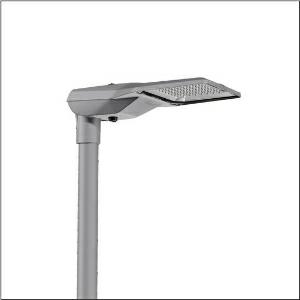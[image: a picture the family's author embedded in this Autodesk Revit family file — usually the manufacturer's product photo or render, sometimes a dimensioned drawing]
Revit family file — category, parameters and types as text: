
# Revit family: streetlight_sl_21_midi___st1_0ab_5xe3m33t08mb_b6c0
name_source: partatom
category: Lighting Fixtures
units: mm (PartAtom-declared; Revit-internal decimal feet)

## family parameters
Cut with Voids When Loaded = No
Host = Face
Light Source = No
Part Type = Normal
Room Calculation Point = No
Round Connector Dimension = Use Diameter
Shared = No

## types (1)
- --- (1 x LED, 16080 lm, 136 W, 3000K)
    Apparent Load = 136 VA
    CIE Flux Codes = 38 73 97 100 100
    Color Rendering = 70
    Color Temperature = 3000K
    Default Elevation = 1800 mm
    Description = Streetlight SL 21 midi, mast luminaire, primary light control with lens, of PMMA, primary optical cover: cover, of toughened safety glass, transparent, light distribution: ST1.0aB, light emission: direct distribution, primary light characteristic: asymmetric, installation type: side-entry, post-top, LED, High Power LED, rated luminous flux: 16.080lm, luminous efficacy: 118lm/W, light colour: 730, colour temperature: 3000K, control gear: D4i, control: flexible luminous flux parameterisation, time-dependent luminous flux control, constant luminous flux control, overheat protection, pre-setting: logarithmic dimming characteristic, mains connection: 230..240V, AC, 50/60Hz, start of lifetime: 136W, end of service life: 142W, reduction: 61W, luminaire housing, of diecast aluminium, powder-coated, Siteco® metallic grey (DB 702S), corrosivity category C5 mid according to DIN EN ISO 12944, please order mast flange separately, inclination adjustable: 0°, 5°, 10°, 15°, sealing non-destructively replaceable, multi-level sealing system, length: 644mm, width: 335mm, height: 110mm, mast flange for spigot size: 42mm (side-entry): 5XC10008XM4, 60/48mm (side-entry/post-top): 5XC10108XM2, 76/60mm (side-entry/post-top): 5XC10108XM1, mounting height: 4..8m, Smart Interface below and above, protection rating (complete): IP66, insulation class (complete): insulation class II (safety insulation), certification: CE, ENEC, ENEC+, VDE, impact resistance: IK10, permissible operating ambient temperature for outdoor applications: -40..+50°C, standard-compliant lighting for roads and squares, packaging unit: 1 piece

Light Distribution: ST1.0aB
    Height = 111 mm
    Lamp = 1 x LED
    Lamp Light Flux = 16080 lm
    Lamp Power = 136 W
    Lamp count = 1
    Length = 644 mm
    Luminous efficacy = 118 lm/W
    Manufacturer = Siteco
    ModVariant = No
    Model = 5XE3M33T08MB
    Number of Poles = 1
    OnlyDefault = Yes
    Power Factor = 1
    Product Name = Streetlight SL 21 midi | ST1.0aB
    Product group = mast luminaire | pylon top
    ProductGroupID = 6100
    Protection Class = Protection class II
    Protection Degree = IP 66
    RLX_Detail_Level = 1
    RLX_Emergency_Light_Flux = 0 lm
    RLX_Emergency_Type = 0
    RLX_Emergency_Type_DB = No
    RlxData = <blob elided: 27037 chars, md5=7a76cc26>
    Socket = socket
    Standby Power = 0 W
    System Light Flux = 16081 lm
    System Power = 136 W
    Type Comments = factory setting: luminous flux: 100 % | dim-lin: 254 | 695 mA
    Type Image = l_1004304.jpg
    URL = http://relux.com
    VarID = @adj_204183
    Voltage = 0 V
    Weight = 0.00 kg
    Width = 336 mm

## geometry (parser evidence)
native form markers: Blend x4, Sweep x10
no freeform markers — native parametric forms only
